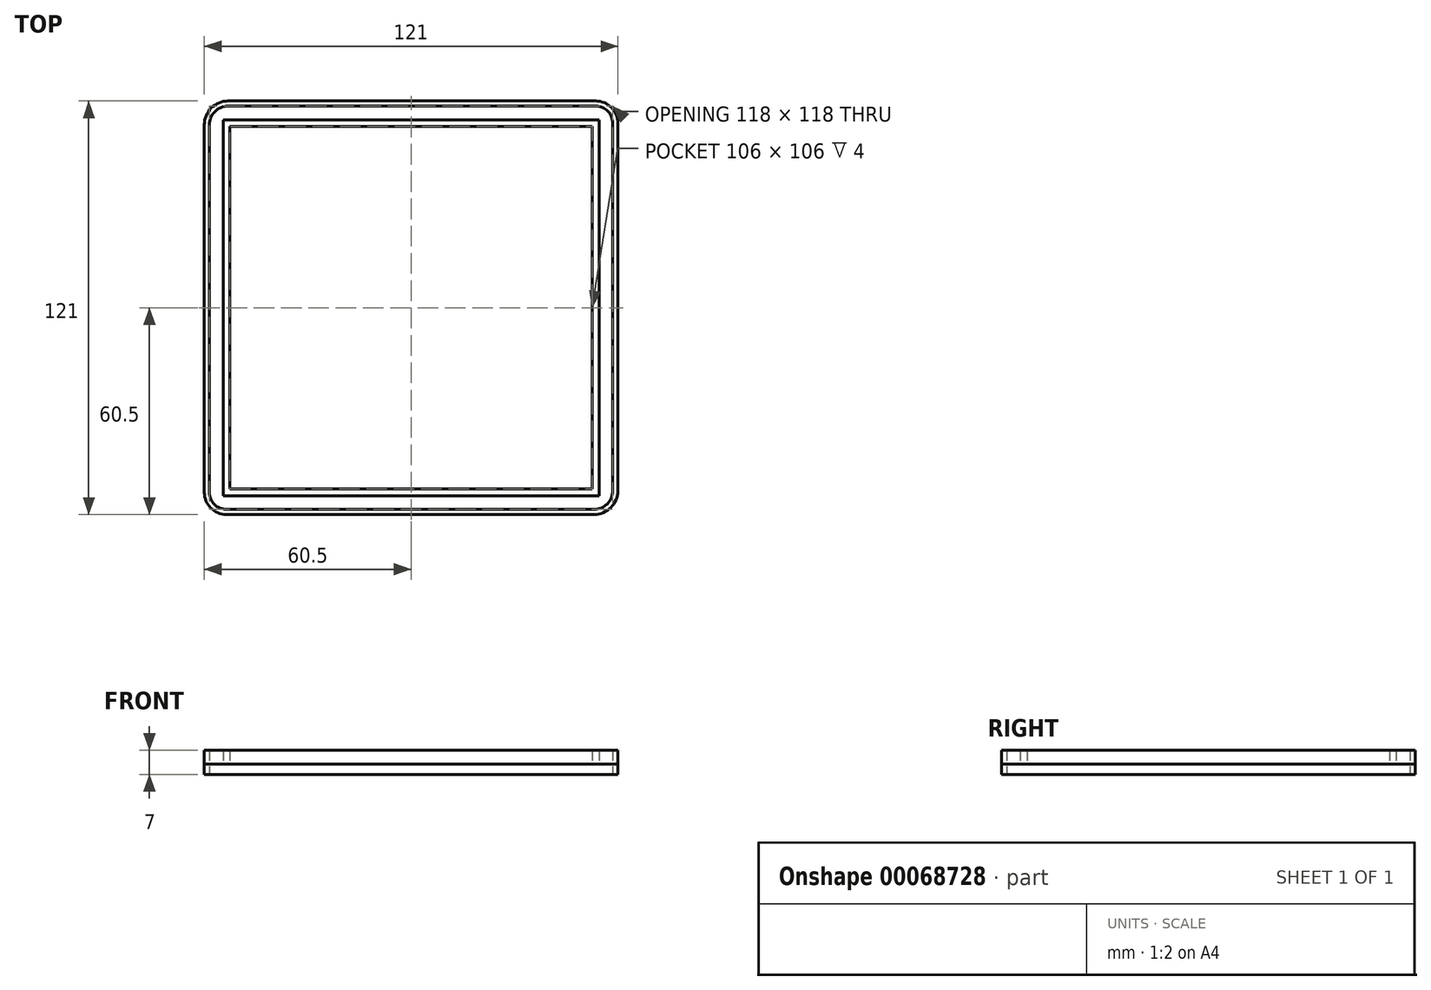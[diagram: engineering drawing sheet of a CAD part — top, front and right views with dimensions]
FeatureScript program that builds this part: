
annotation { "Feature Type Name" : "Feature", "Feature Type Description" : "" }
export const myFeature = defineFeature(function(context is Context, id is Id, definition is map)
    precondition{}
    {
        {
            var Q0;
            Q0=qCreatedBy(makeId("Top.planeOp"),FACE);
            var sketch = newSketch(context, id + "F0", { "sketchPlane" : qUnion([Q0])});
            skArc(sketch, "E0.0", {"start": v(-53.5, 59) * mm, "mid": v(-57.4, 57.4) * mm, "end": v(-59, 53.5) * mm});
            skLineSegment(sketch, "E0.1", {"start": v(-53.5, 59) * mm, "end": v(54, 59) * mm});
            skLineSegment(sketch, "E0.2", {"start": v(-55, 55) * mm, "end": v(55, 55) * mm});
            skLineSegment(sketch, "E0.4", {"start": v(-55, -55) * mm, "end": v(55, -55) * mm});
            skArc(sketch, "E0.6", {"start": v(59, 54) * mm, "mid": v(57.54, 57.54) * mm, "end": v(54, 59) * mm});
            skLineSegment(sketch, "E0.7", {"start": v(59, 54) * mm, "end": v(59, -53.5) * mm});
            skArc(sketch, "E0.8", {"start": v(53.5, -59) * mm, "mid": v(57.4, -57.4) * mm, "end": v(59, -53.5) * mm});
            skLineSegment(sketch, "E0.9", {"start": v(-54, -59) * mm, "end": v(53.5, -59) * mm});
            skLineSegment(sketch, "E0.10", {"start": v(-59, 53.5) * mm, "end": v(-59, -54) * mm});
            skArc(sketch, "E0.11", {"start": v(-59, -54) * mm, "mid": v(-57.54, -57.54) * mm, "end": v(-54, -59) * mm});
            skLineSegment(sketch, "E1.0", {"start": v(60.5, 54) * mm, "end": v(60.5, -53.5) * mm});
            skArc(sketch, "E1.1", {"start": v(53.5, -60.5) * mm, "mid": v(58.45, -58.45) * mm, "end": v(60.5, -53.5) * mm});
            skArc(sketch, "E1.2", {"start": v(60.5, 54) * mm, "mid": v(58.6, 58.6) * mm, "end": v(54, 60.5) * mm});
            skLineSegment(sketch, "E1.3", {"start": v(-54, -60.5) * mm, "end": v(53.5, -60.5) * mm});
            skLineSegment(sketch, "E1.4", {"start": v(-53.5, 60.5) * mm, "end": v(54, 60.5) * mm});
            skArc(sketch, "E1.5", {"start": v(-53.5, 60.5) * mm, "mid": v(-58.45, 58.45) * mm, "end": v(-60.5, 53.5) * mm});
            skLineSegment(sketch, "E1.6", {"start": v(-60.5, 53.5) * mm, "end": v(-60.5, -54) * mm});
            skArc(sketch, "E1.7", {"start": v(-60.5, -54) * mm, "mid": v(-58.6, -58.6) * mm, "end": v(-54, -60.5) * mm});
            skLineSegment(sketch, "E2", {"start": v(55, -55) * mm, "end": v(55, 55) * mm});
            skLineSegment(sketch, "E3", {"start": v(-55, 55) * mm, "end": v(-55, -55) * mm});
            skLineSegment(sketch, "E4.0", {"start": v(53, -53) * mm, "end": v(53, 53) * mm});
            skLineSegment(sketch, "E4.1", {"start": v(-53, -53) * mm, "end": v(53, -53) * mm});
            skLineSegment(sketch, "E4.2", {"start": v(-53, 53) * mm, "end": v(-53, -53) * mm});
            skLineSegment(sketch, "E4.3", {"start": v(-53, 53) * mm, "end": v(53, 53) * mm});
            skLineSegment(sketch, "E5", {"start": v(53, 53) * mm, "end": v(55, 55) * mm});
            skLineSegment(sketch, "E6", {"start": v(53, -53) * mm, "end": v(55, -55) * mm});
            skLineSegment(sketch, "E7", {"start": v(-53, -53) * mm, "end": v(-55, -55) * mm});
            skLineSegment(sketch, "E8", {"start": v(-53, 53) * mm, "end": v(-55, 55) * mm});
            skSolve(sketch);
        }
        {
            var Q0;
            Q0=makeQuery(id+"F0.imprint","IMPRINT",FACE,{"disambiguationData":[TD([[makeQuery(id+"F0.imprint","IMPRINT",EDGE,{"derivedFrom":sQuery(id+"F0.wireOp",EDGE,"E0.4")}),1.0]])]});
            var Q1;
            Q1=makeQuery(id+"F0.imprint","IMPRINT",FACE,{"disambiguationData":[TD([[makeQuery(id+"F0.imprint","IMPRINT",EDGE,{"derivedFrom":sQuery(id+"F0.wireOp",EDGE,"E3")}),1.0]])]});
            var Q2;
            Q2=makeQuery(id+"F0.imprint","IMPRINT",FACE,{"disambiguationData":[TD([[makeQuery(id+"F0.imprint","IMPRINT",EDGE,{"derivedFrom":sQuery(id+"F0.wireOp",EDGE,"E0.2")}),-1.0]])]});
            var Q3;
            Q3=makeQuery(id+"F0.imprint","IMPRINT",FACE,{"disambiguationData":[TD([[makeQuery(id+"F0.imprint","IMPRINT",EDGE,{"derivedFrom":sQuery(id+"F0.wireOp",EDGE,"E2")}),1.0]])]});
            var Q4;
            Q4=makeQuery(id+"F0.imprint","IMPRINT",FACE,{"disambiguationData":[TD([[makeQuery(id+"F0.imprint","IMPRINT",EDGE,{"derivedFrom":sQuery(id+"F0.wireOp",EDGE,"E0.0")}),1.0]])]});
            var Q5;
            Q5=makeQuery(id+"F0.imprint","IMPRINT",FACE,{"disambiguationData":[TD([[makeQuery(id+"F0.imprint","IMPRINT",EDGE,{"derivedFrom":sQuery(id+"F0.wireOp",EDGE,"E4.0")}),1.0]])]});
            var Q6;
            Q6=makeQuery(id+"F0.imprint","IMPRINT",FACE,{"disambiguationData":[TD([[makeQuery(id+"F0.imprint","IMPRINT",EDGE,{"derivedFrom":sQuery(id+"F0.wireOp",EDGE,"E0.0")}),-1.0]])]});
            extrude(context, id + "F1", {"entities" : qUnion([Q0, Q1, Q2, Q3, Q4, Q5, Q6]), "depth" : 3 * mm});
        }
        {
            var Q0;
            Q0=makeQuery(id+"F0.imprint","IMPRINT",FACE,{"disambiguationData":[TD([[makeQuery(id+"F0.imprint","IMPRINT",EDGE,{"derivedFrom":sQuery(id+"F0.wireOp",EDGE,"E0.0")}),-1.0]])]});
            extrude(context, id + "F2", {"entities" : qUnion([Q0]), "depth" : 7 * mm});
        }
        {
            var Q0;
            Q0=makeQuery(id+"F0.imprint","IMPRINT",FACE,{"disambiguationData":[TD([[makeQuery(id+"F0.imprint","IMPRINT",EDGE,{"derivedFrom":sQuery(id+"F0.wireOp",EDGE,"E0.2")}),-1.0]])]});
            var Q1;
            Q1=makeQuery(id+"F0.imprint","IMPRINT",FACE,{"disambiguationData":[TD([[makeQuery(id+"F0.imprint","IMPRINT",EDGE,{"derivedFrom":sQuery(id+"F0.wireOp",EDGE,"E0.4")}),1.0]])]});
            var Q2;
            Q2=makeQuery(id+"F0.imprint","IMPRINT",FACE,{"disambiguationData":[TD([[makeQuery(id+"F0.imprint","IMPRINT",EDGE,{"derivedFrom":sQuery(id+"F0.wireOp",EDGE,"E3")}),1.0]])]});
            var Q3;
            Q3=makeQuery(id+"F0.imprint","IMPRINT",FACE,{"disambiguationData":[TD([[makeQuery(id+"F0.imprint","IMPRINT",EDGE,{"derivedFrom":sQuery(id+"F0.wireOp",EDGE,"E2")}),1.0]])]});
            extrude(context, id + "F3", {"entities" : qUnion([Q0, Q1, Q2, Q3]), "operationType" : NewBodyOperationType.ADD, "depth" : 7 * mm});
        }
    });
